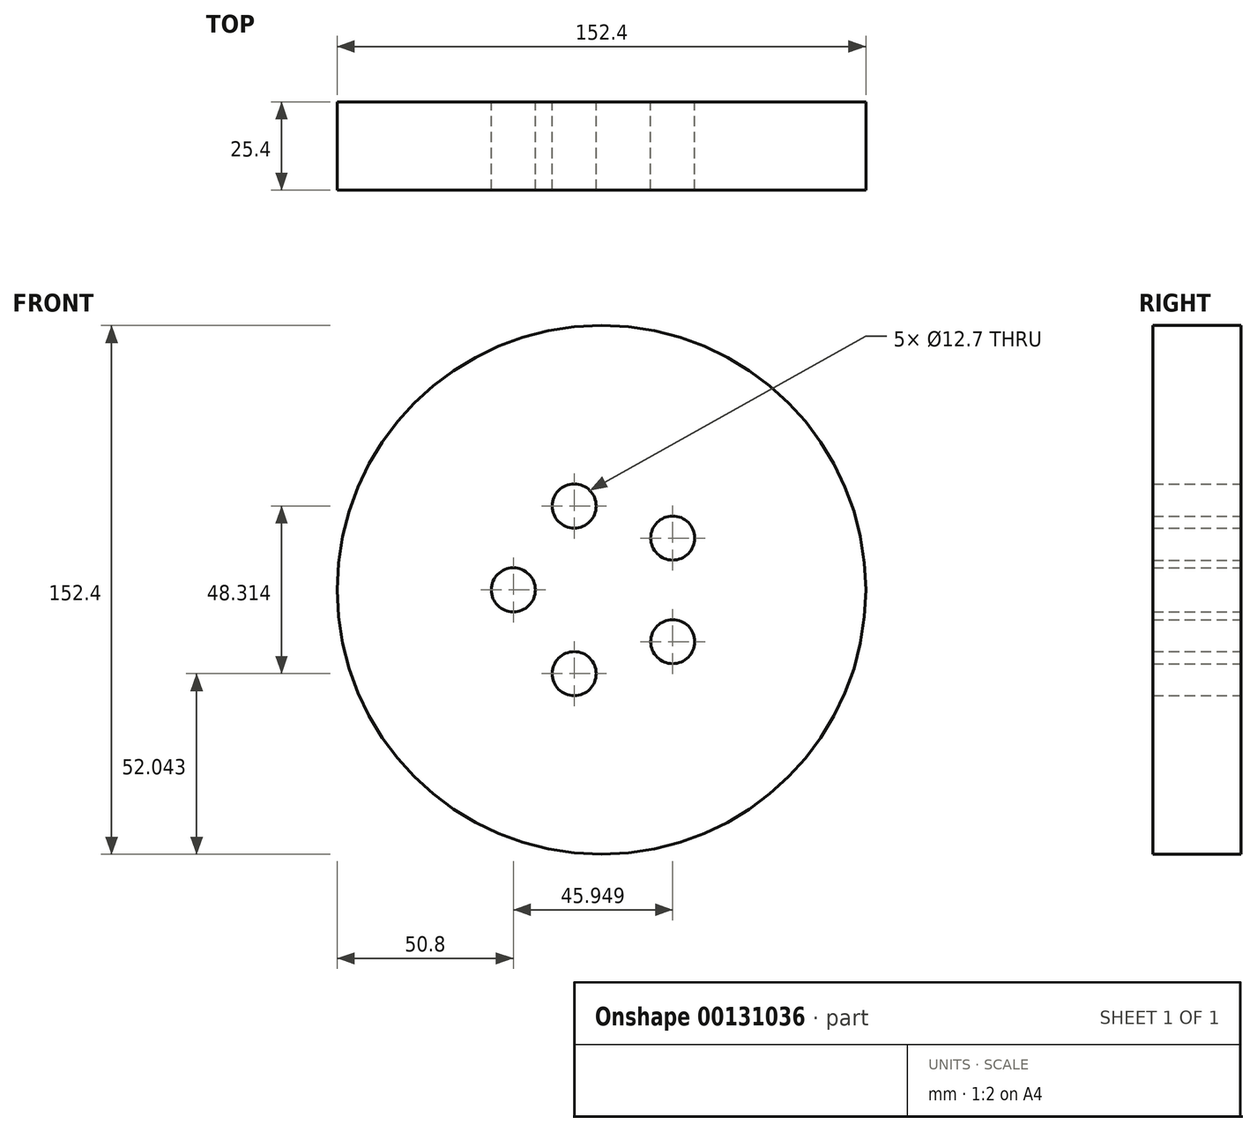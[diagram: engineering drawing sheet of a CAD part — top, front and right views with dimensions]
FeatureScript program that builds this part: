
annotation { "Feature Type Name" : "Feature", "Feature Type Description" : "" }
export const myFeature = defineFeature(function(context is Context, id is Id, definition is map)
    precondition{}
    {
        {
            var Q0;
            Q0=qCreatedBy(makeId("Front.planeOp"),FACE);
            var sketch = newSketch(context, id + "F0", { "sketchPlane" : qUnion([Q0])});
            skCircle(sketch, "E0", {"center": v(0, 0) * mm, "radius": 76.2 * mm});
            skCircle(sketch, "E1", {"center": v(-25.4, 0) * mm, "radius": 6.35 * mm});
            skCircle(sketch, "E2.1.0", {"center": v(-7.85, -24.16) * mm, "radius": 6.35 * mm});
            skCircle(sketch, "E2.2.0", {"center": v(20.55, -14.93) * mm, "radius": 6.35 * mm});
            skCircle(sketch, "E2.3.0", {"center": v(20.55, 14.93) * mm, "radius": 6.35 * mm});
            skCircle(sketch, "E2.4.0", {"center": v(-7.85, 24.16) * mm, "radius": 6.35 * mm});
            skSolve(sketch);
        }
        {
            var Q0;
            Q0=makeQuery(id+"F0.imprint","IMPRINT",FACE,{"disambiguationData":[TD([[makeQuery(id+"F0.imprint","IMPRINT",EDGE,{"derivedFrom":sQuery(id+"F0.wireOp",EDGE,"E2.4.0")}),1.0]])]});
            var Q1;
            Q1=makeQuery(id+"F0.imprint","IMPRINT",FACE,{"disambiguationData":[TD([[makeQuery(id+"F0.imprint","IMPRINT",EDGE,{"derivedFrom":sQuery(id+"F0.wireOp",EDGE,"E2.1.0")}),1.0]])]});
            var Q2;
            Q2=makeQuery(id+"F0.imprint","IMPRINT",FACE,{"disambiguationData":[TD([[makeQuery(id+"F0.imprint","IMPRINT",EDGE,{"derivedFrom":sQuery(id+"F0.wireOp",EDGE,"E2.3.0")}),1.0]])]});
            var Q3;
            Q3=makeQuery(id+"F0.imprint","IMPRINT",FACE,{"disambiguationData":[TD([[makeQuery(id+"F0.imprint","IMPRINT",EDGE,{"derivedFrom":sQuery(id+"F0.wireOp",EDGE,"E2.2.0")}),1.0]])]});
            var Q4;
            Q4=makeQuery(id+"F0.imprint","IMPRINT",FACE,{"disambiguationData":[TD([[makeQuery(id+"F0.imprint","IMPRINT",EDGE,{"derivedFrom":sQuery(id+"F0.wireOp",EDGE,"E1")}),1.0]])]});
            extrude(context, id + "F1", {"entities" : qUnion([Q0, Q1, Q2, Q3, Q4]), "depth" : 25.4 * mm});
        }
        {
            var Q0;
            Q0 = qSketchRegion(id + "F0", true);
            extrude(context, id + "F2", {"entities" : qUnion([Q0]), "depth" : 25.4 * mm});
        }
    });
